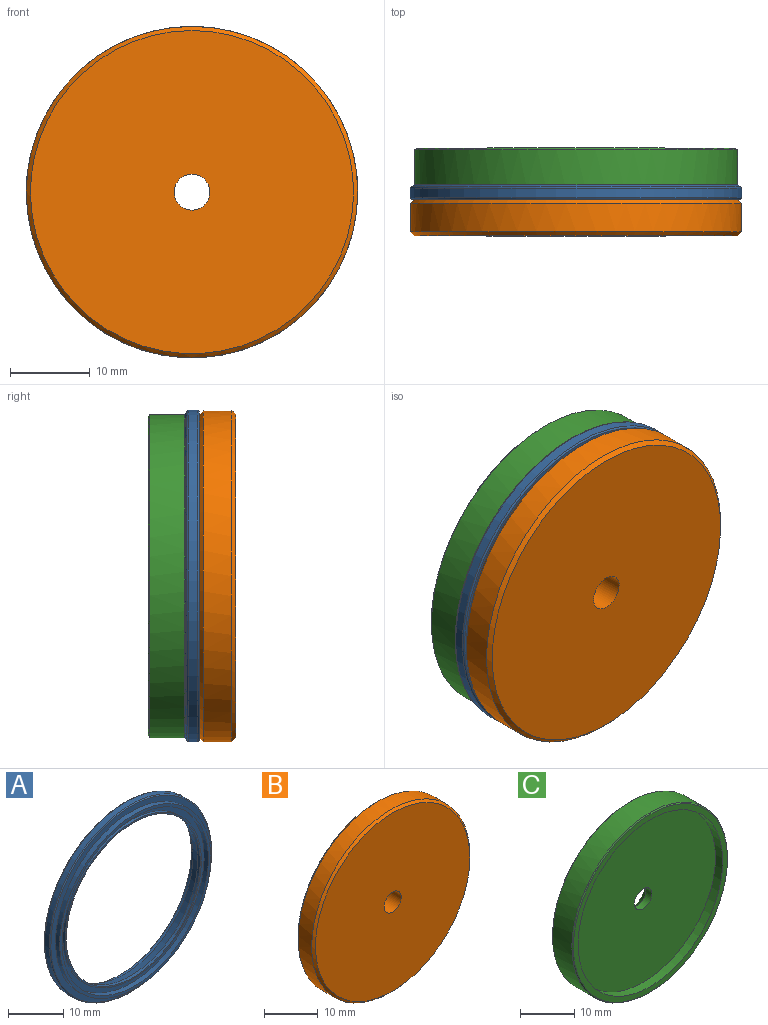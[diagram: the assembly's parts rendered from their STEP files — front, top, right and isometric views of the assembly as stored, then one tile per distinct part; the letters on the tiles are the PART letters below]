
ASSEMBLY  parts=3 mates=2
PART A: 22 faces, bbox 44.9x3.8x44.9 mm
  f0: cylinder r=18.75mm len=37.5mm, axis (0,1,0), area 129.6mm2, adj f1,f21
  f1: plane 38.7x38.7mm, normal (0,-1,0), area 71.8mm2, adj f0,f2
  f2: cylinder r=19.35mm len=38.7mm, axis (0,1,0), area 127.7mm2, adj f1,f3
  f3: plane 41.1x41.1mm, normal (0,-1,0), area 150.4mm2, adj f2,f4
  f4: torus R=20.55mm, axis (0,1,0), area 40.8mm2, adj f3,f5
  f5: cylinder r=20.75mm len=41.5mm, axis (0,1,0), area 155.5mm2, adj f4,f6
  f6: torus R=20.55mm, axis (0,1,0), area 25.6mm2, adj f5,f7
  f7: cone r=20.3mm half-angle=56.3deg, axis (0,-1,0), area 55.4mm2, adj f6,f8
  f8: torus R=20.28mm, axis (0,1,0), area 13.7mm2, adj f7,f9
  f9: cylinder r=20.23mm len=40.45mm, axis (0,1,0), area 96.1mm2, adj f8,f10
  f10: plane 40.45x40.45mm, normal (0,1,0), area 180.6mm2, adj f9,f11
  f11: cylinder r=18.75mm len=37.5mm, axis (0,1,0), area 106mm2, adj f10,f12
  f12: cone r=18.29mm half-angle=28.6deg, axis (0,-1,0), area 112.6mm2, adj f11,f13
  f13: plane 36.57x36.57mm, normal (0,1,0), area 9.9mm2, adj f12,f14
  f14: cylinder r=18.2mm len=36.4mm, axis (0,1,0), area 97.2mm2, adj f13,f15
  f15: cone r=18.2mm half-angle=30deg, axis (0,-1,0), area 19.9mm2, adj f14,f16
  f16: plane 36.57x36.57mm, normal (0,1,0), area 71.9mm2, adj f15,f17
  f17: cone r=17.15mm half-angle=16.9deg, axis (0,1,0), area 188.5mm2, adj f16,f18
  f18: cylinder r=17.15mm len=34.3mm, axis (0,1,0), area 70mm2, adj f17,f19
  f19: plane 34.9x34.9mm, normal (0,-1,0), area 32.6mm2, adj f18,f20
  f20: cylinder r=17.45mm len=34.9mm, axis (0,1,0), area 65.8mm2, adj f19,f21
  f21: plane 37.5x37.5mm, normal (0,-1,0), area 147.8mm2, adj f0,f20
PART B: 10 faces, bbox 41.5x4.6x41.5 mm
  f0: cylinder r=19.35mm len=38.7mm, axis (0,-1,0), area 127.7mm2, adj f1,f6
  f1: plane 38.7x38.7mm, normal (0,1,0), area 80.6mm2, adj f0,f2
  f2: cylinder r=18.68mm len=37.35mm, axis (0,-1,0), area 41.1mm2, adj f1,f3
  f3: plane 37.35x37.35mm, normal (0,1,0), area 1079.7mm2, adj f2,f9
  f4: plane 40.45x40.45mm, normal (0,-1,0), area 1269.2mm2, adj f7,f9
  f5: cylinder r=20.73mm len=41.45mm, axis (0,-1,0), area 462.3mm2, adj f7,f8
  f6: plane 40.45x40.45mm, normal (0,1,0), area 108.8mm2, adj f0,f8
  f7: cone r=20.23mm half-angle=45deg, axis (0,1,0), area 91mm2, adj f4,f5
  f8: cone r=20.73mm half-angle=45deg, axis (0,-1,0), area 91mm2, adj f5,f6
  f9: cylinder r=2.25mm len=4.5mm, axis (0,1,0), area 54.4mm2, adj f3,f4
PART C: 9 faces, bbox 40.5x5.4x40.5 mm
  f0: plane 37.6x37.6mm, normal (0,-1,0), area 1094.5mm2, adj f1,f7
  f1: cylinder r=18.8mm len=37.6mm, axis (0,-1,0), area 223.8mm2, adj f0,f2
  f2: plane 40.05x40.05mm, normal (0,-1,0), area 149.4mm2, adj f1,f6
  f3: cylinder r=20.23mm len=40.45mm, axis (0,-1,0), area 636.4mm2, adj f5,f6
  f4: plane 40.05x40.05mm, normal (0,1,0), area 1203mm2, adj f5,f8
  f5: cone r=20.23mm half-angle=45deg, axis (0,-1,0), area 35.8mm2, adj f3,f4
  f6: cone r=20.03mm half-angle=45deg, axis (0,1,0), area 35.8mm2, adj f2,f3
  f7: cylinder r=2.25mm len=4.5mm, axis (0,1,0), area 21.4mm2, adj f0,f8
  f8: cone r=2.25mm half-angle=45deg, axis (0,1,0), area 57.8mm2, adj f4,f7
PLACE A t=(-10.54,-10.66,4.21)mm
PLACE B t=(-8.34,-11.66,4.21)mm fixed
PLACE C t=(-8.89,-10.66,4.21)mm
MATE fastened A.f0 <-> C.f7  axis (0,1,0) through (-27.69,-10.66,4.21)mm
MATE fastened B.f0 <-> A.f0  axis (0,1,0) through (-27.69,-11.66,4.21)mm
